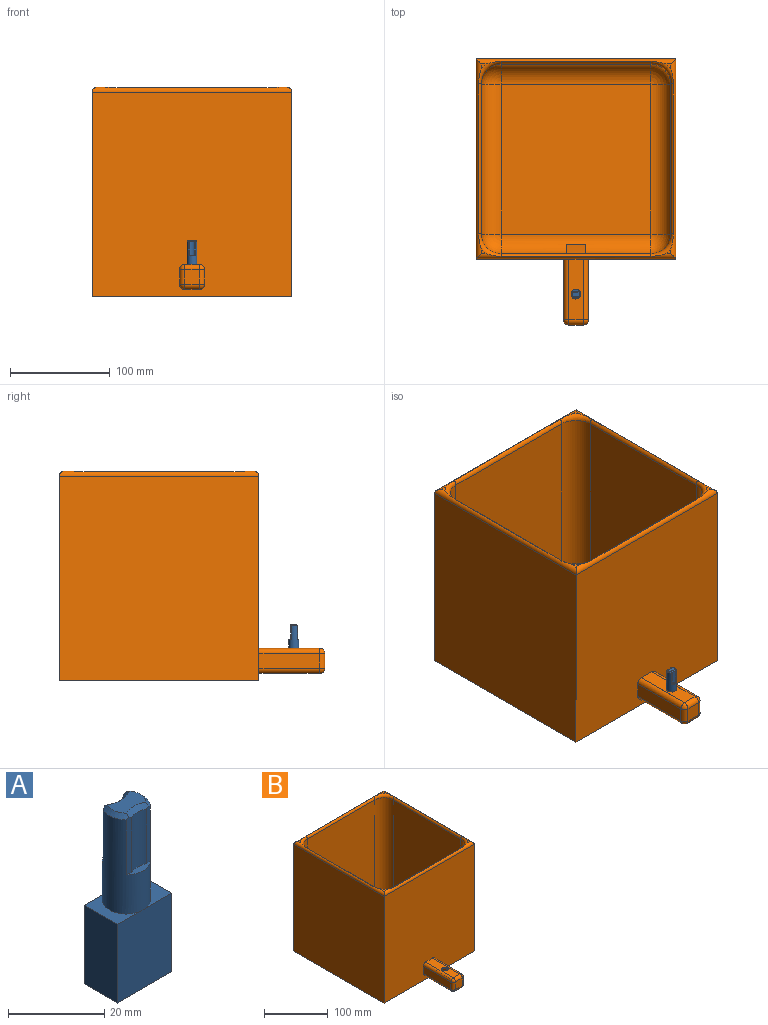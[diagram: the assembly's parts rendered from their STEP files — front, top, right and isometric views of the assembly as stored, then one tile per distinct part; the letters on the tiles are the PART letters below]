
ASSEMBLY  parts=2 mates=1
PART A: 23 faces, bbox 16x10x45 mm
  f0: plane 7.07x1.84mm, normal (0,0,1), area 7.8mm2, adj f4,f12,f19,f20
  f1: plane 8.33x2.75mm, normal (0,0,1), area 14mm2, adj f4,f13,f21,f22
  f2: plane 1.99x0.1mm, normal (0,0,-1), area 0.1mm2, adj f4,f11
  f3: plane 1.99x0.1mm, normal (0,0,-1), area 0.1mm2, adj f4,f10
  f4: cylinder r=5mm len=24mm, axis (0,0,1), area 506mm2, adj f0,f1,f2,f3,f5,f6,f15,f18
  f5: plane 9.8x6.51mm, normal (0,0,1), area 34.4mm2, adj f4,f7,f10,f11
  f6: plane 9.8x7.51mm, normal (0,0,1), area 44.2mm2, adj f4,f9,f10,f11
  f7: plane 20x9.8mm, normal (-1,0,0), area 196mm2, adj f5,f8,f10,f11
  f8: plane 16x9.8mm, normal (0,0,-1), area 156.8mm2, adj f7,f9,f10,f11
  f9: plane 20x9.8mm, normal (1,0,0), area 196mm2, adj f6,f8,f10,f11
  f10: plane 20x16mm, normal (0,-1,0), area 320mm2, adj f3,f5,f6,f7,f8,f9
  f11: plane 20x16mm, normal (0,1,0), area 320mm2, adj f2,f5,f6,f7,f8,f9
  f12: cylinder r=5mm len=14mm, axis (0,0,-1), area 67mm2, adj f0,f16,f19,f20
  f13: cylinder r=5mm len=14mm, axis (0,0,-1), area 80.4mm2, adj f1,f17,f21,f22
  f14: plane 8x5.31mm, normal (0,0,1), area 30.7mm2, adj f15,f16,f17,f18
  f15: cone r=4mm half-angle=45deg, axis (0,0,-1), area 9.1mm2, adj f4,f14,f16,f17,f20,f22
  f16: cone r=5mm half-angle=45deg, axis (0,0,1), area 8.2mm2, adj f12,f14,f15,f18,f19,f20
  f17: cone r=5mm half-angle=45deg, axis (0,0,1), area 9.7mm2, adj f13,f14,f15,f18,f21,f22
  f18: cone r=4mm half-angle=45deg, axis (0,0,-1), area 9.9mm2, adj f4,f14,f16,f17,f19,f21
  f19: plane 14.4x1.26mm, normal (0.15,-0.99,0), area 17.7mm2, adj f0,f4,f12,f16,f18
  f20: plane 14.4x1.27mm, normal (-0.15,-0.99,0), area 17.7mm2, adj f0,f4,f12,f15,f16
  f21: plane 14.56x1.51mm, normal (0.14,0.99,0), area 21.2mm2, adj f1,f4,f13,f17,f18
  f22: plane 14.56x1.48mm, normal (-0.26,0.96,0), area 21.2mm2, adj f1,f4,f13,f15,f17
PART B: 66 faces, bbox 211.8x271.9x210 mm
  f0: plane 5x5mm, normal (0,0,1), area 11.3mm2, adj f59,f60,f63
  f1: plane 5x5mm, normal (0,0,1), area 11.3mm2, adj f55,f58,f59
  f2: plane 5x5mm, normal (0,0,1), area 11.3mm2, adj f62,f63,f65
  f3: plane 15x1.2mm, normal (0,0,-1), area 18mm2, adj f33,f34,f35,f37
  f4: plane 47x15mm, normal (0,0,-1), area 705mm2, adj f5,f22,f31,f32
  f5: plane 205x200mm, normal (0,-1,0), area 40396.5mm2, adj f4,f6,f11,f13,f16,f17,f18,f20
  f6: plane 200x200mm, normal (0,0,-1), area 40000mm2, adj f5,f11,f12,f13
  f7: plane 178x150mm, normal (-1,0,0), area 26700mm2, adj f44,f50,f53,f56
  f8: plane 178x150mm, normal (0,-1,0), area 26700mm2, adj f47,f51,f53,f64
  f9: plane 178x150mm, normal (1,0,0), area 26700mm2, adj f42,f46,f47,f61
  f10: plane 178x150mm, normal (0,1,0), area 26640mm2, adj f38,f39,f40,f42,f44,f45,f54
  f11: plane 205x200mm, normal (1,0,0), area 41000mm2, adj f5,f6,f12,f59
  f12: plane 205x200mm, normal (0,1,0), area 41000mm2, adj f6,f11,f13,f63
  f13: plane 205x200mm, normal (-1,0,0), area 41000mm2, adj f5,f6,f12,f62
  f14: plane 5x5mm, normal (0,0,1), area 11.3mm2, adj f57,f58,f62
  f15: plane 150x150mm, normal (0,0,1), area 22500mm2, adj f45,f46,f50,f51
  f16: plane 61x15mm, normal (1,0,0), area 915mm2, adj f5,f25,f29,f31
  f17: plane 61x15mm, normal (0,0,1), area 836.5mm2, adj f5,f20,f24,f25,f41
  f18: plane 61x15mm, normal (-1,0,0), area 915mm2, adj f5,f20,f22,f23
  f19: plane 15x15mm, normal (0,-1,0), area 225mm2, adj f23,f24,f28,f29
  f20: cylinder r=5mm len=61mm, axis (0,-1,0), area 479.1mm2, adj f5,f17,f18,f21
  f21: sphere r=5mm, area 39.3mm2, adj f20,f23,f24
  f22: cylinder r=5mm len=61mm, axis (0,1,0), area 479.1mm2, adj f4,f5,f18,f26,f35
  f23: cylinder r=5mm len=15mm, axis (0,0,1), area 117.8mm2, adj f18,f19,f21,f26
  f24: cylinder r=5mm len=15mm, axis (1,0,0), area 117.8mm2, adj f17,f19,f21,f27
  f25: cylinder r=5mm len=61mm, axis (0,1,0), area 479.1mm2, adj f5,f16,f17,f27
  f26: sphere r=5mm, area 39.3mm2, adj f22,f23,f28,f35
  f27: sphere r=5mm, area 39.3mm2, adj f24,f25,f29
  f28: cylinder r=5mm len=15mm, axis (-1,0,0), area 102.7mm2, adj f19,f26,f30,f34
  f29: cylinder r=5mm len=15mm, axis (0,0,-1), area 117.8mm2, adj f16,f19,f27,f30
  f30: sphere r=5mm, area 39.3mm2, adj f28,f29,f31,f33
  f31: cylinder r=5mm len=61mm, axis (0,-1,0), area 479.1mm2, adj f4,f5,f16,f30,f33
  f32: plane 15x2.5mm, normal (0,-1,0), area 37.5mm2, adj f4,f33,f35,f36
  f33: plane 18.4x15mm, normal (-1,0,0), area 56.5mm2, adj f3,f30,f31,f32,f34,f36,f37
  f34: plane 18.3x15mm, normal (0,1,0), area 274.5mm2, adj f3,f28,f33,f35
  f35: plane 18.4x15mm, normal (1,0,0), area 56.5mm2, adj f3,f22,f26,f32,f34,f36,f37
  f36: plane 75.26x20mm, normal (0,0,1), area 1298.3mm2, adj f32,f33,f35,f37,f38,f40,f45
  f37: plane 20x20mm, normal (0,1,0), area 161.5mm2, adj f3,f33,f35,f36,f38,f39,f40
  f38: plane 75.26x20mm, normal (1,0,0), area 1363.2mm2, adj f10,f36,f37,f39,f45
  f39: plane 65.8x20mm, normal (0,0,-1), area 1237.5mm2, adj f10,f37,f38,f40,f41
  f40: plane 75.26x20mm, normal (-1,0,0), area 1363.2mm2, adj f10,f36,f37,f39,f45
  f41: cylinder r=5mm len=10mm, axis (0,0,1), area 78.5mm2, adj f17,f39
  f42: cylinder r=20mm len=178mm, axis (0,0,1), area 5592mm2, adj f9,f10,f43,f57
  f43: sphere r=20mm, area 628.3mm2, adj f42,f45,f46
  f44: cylinder r=20mm len=178mm, axis (0,0,-1), area 5592mm2, adj f7,f10,f48,f55
  f45: cylinder r=20mm len=150mm, axis (-1,0,0), area 4306mm2, adj f10,f15,f36,f38,f40,f43,f48
  f46: cylinder r=20mm len=150mm, axis (0,1,0), area 4712.4mm2, adj f9,f15,f43,f49
  f47: cylinder r=20mm len=178mm, axis (0,0,-1), area 5592mm2, adj f8,f9,f49,f65
  f48: sphere r=20mm, area 628.3mm2, adj f44,f45,f50
  f49: sphere r=20mm, area 628.3mm2, adj f46,f47,f51
  f50: cylinder r=20mm len=150mm, axis (0,-1,0), area 4712.4mm2, adj f7,f15,f48,f52
  f51: cylinder r=20mm len=150mm, axis (1,0,0), area 4712.4mm2, adj f8,f15,f49,f52
  f52: sphere r=20mm, area 628.3mm2, adj f50,f51,f53
  f53: cylinder r=20mm len=178mm, axis (0,0,1), area 5592mm2, adj f7,f8,f52,f60
  f54: cylinder r=5mm len=150mm, axis (1,0,0), area 785.4mm2, adj f10,f55,f57,f58
  f55: torus R=25mm, axis (0,0,1), area 215.4mm2, adj f1,f44,f54,f56,f58,f59
  f56: cylinder r=5mm len=150mm, axis (0,1,0), area 785.4mm2, adj f7,f55,f59,f60
  f57: torus R=25mm, axis (0,0,1), area 215.4mm2, adj f14,f42,f54,f58,f61,f62
  f58: cylinder r=5mm len=200mm, axis (-1,0,0), area 1098mm2, adj f1,f5,f14,f54,f55,f57,f59,f62
  f59: cylinder r=5mm len=200mm, axis (0,-1,0), area 1098mm2, adj f0,f1,f11,f55,f56,f58,f60,f63
  f60: torus R=25mm, axis (0,0,1), area 215.4mm2, adj f0,f53,f56,f59,f63,f64
  f61: cylinder r=5mm len=150mm, axis (0,-1,0), area 785.4mm2, adj f9,f57,f62,f65
  f62: cylinder r=5mm len=200mm, axis (0,1,0), area 1098mm2, adj f2,f13,f14,f57,f58,f61,f63,f65
  f63: cylinder r=5mm len=200mm, axis (1,0,0), area 1098mm2, adj f0,f2,f12,f59,f60,f62,f64,f65
  f64: cylinder r=5mm len=150mm, axis (-1,0,0), area 785.4mm2, adj f8,f60,f63,f65
  f65: torus R=25mm, axis (0,0,1), area 215.4mm2, adj f2,f47,f61,f62,f63,f64
PLACE A t=(-179.02,-179.81,-63.79)mm
PLACE B t=(-179.02,-44.81,-75.29)mm
MATE revolute A.f4 <-> B.f41  axis (0,0,1) through (-179.02,-179.81,-43.79)mm
